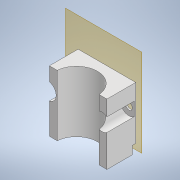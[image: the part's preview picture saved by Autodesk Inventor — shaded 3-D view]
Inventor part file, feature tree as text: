
AUTODESK INVENTOR PART (.ipt)
format: ipt  version: 2020.2 (Build 242310000, 310)  size: 177,664 bytes
history: native  units: mm
features: reference x6, sketch x5, extrude x5, other x4, plane x3, projected_geometry x1
ambient origin geometry x8: Origin, YZ Plane, XZ Plane, XY Plane, X Axis, Y Axis, Z Axis, Center Point
bodies: Solid1 (feature_tree)
feature tree (24):
  sketch  "Sketch1"  dims[d0=0.4mm d1=10.0mm d2=0.0mm]
  plane  "Work Plane1"
  extrude  "Extrusion1"  Depth=10.0mm TaperAngle=0.0deg
  extrude  "Extrusion2"  Depth=34.0mm
  extrude  "Extrusion3"  Depth=24.0mm
  plane  "Work Plane2"
  plane  "Work Plane3"
  extrude  "Extrusion4"  Depth=36.0mm
  extrude  "Extrusion5"  Depth=3.0mm
  reference  "Reference1"
  sketch  "Sketch2"  dims[d10=17.0mm d11=0.0mm d12=34.0mm]
  reference  "Reference2"
  reference  "Reference3"
  projected_geometry  "Projected Loop1"
  sketch  "Sketch4"  dims[d13=4.0mm d14=24.0mm]
  reference  "Reference4"
  sketch  "Sketch5"  dims[d15=5.0mm d16=36.0mm]
  reference  "Reference5"
  reference  "Reference6"
  sketch  "Sketch6"  dims[d17=3.0mm d18=3.0mm d19=1.5mm d20=10.0mm d21=0.0mm d22=14.0mm d23=7.0mm d24=3.64985mm d25=1.0mm d26=0.0mm d27=4.0mm d28=0.0mm]
  other  "<userpath>\OneDrive\Apps\0011_VentControlValve\Drawings\Assembly.iam"
  other  "Assembly.iam"
  other  "center Section:1"
  other  "motor+Gearbox:1"
